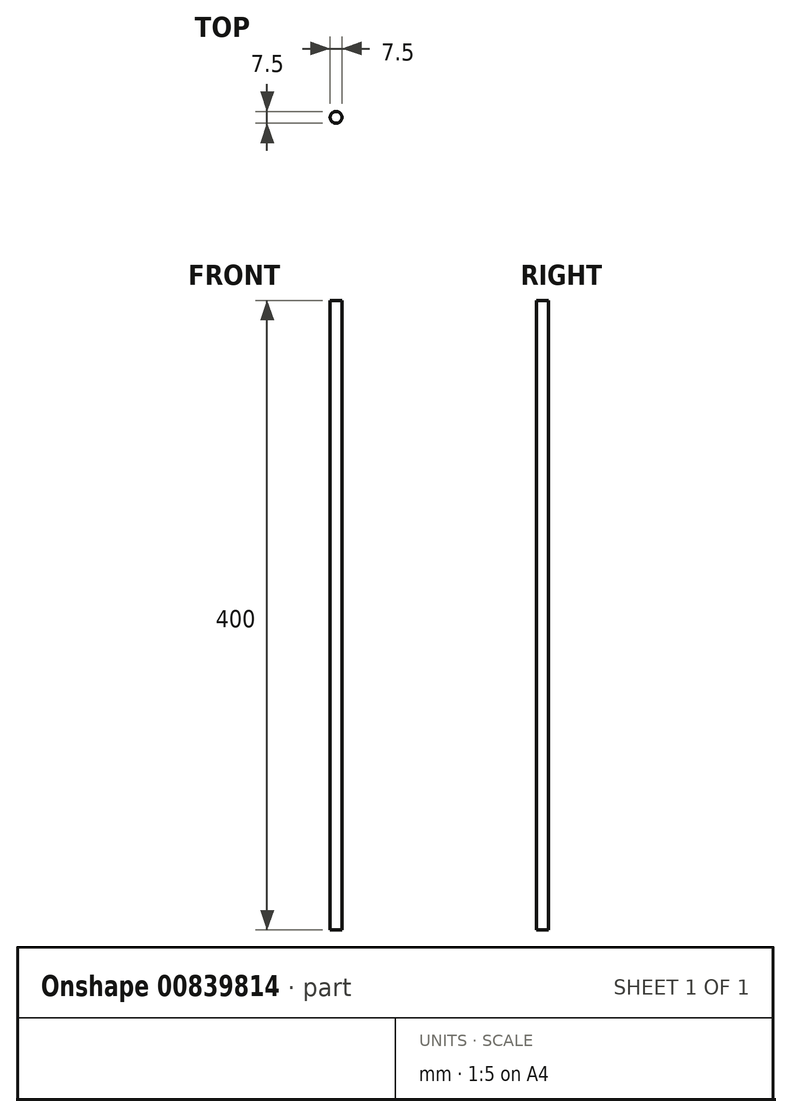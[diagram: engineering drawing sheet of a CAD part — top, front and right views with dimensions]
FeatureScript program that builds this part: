
annotation { "Feature Type Name" : "Feature", "Feature Type Description" : "" }
export const myFeature = defineFeature(function(context is Context, id is Id, definition is map)
    precondition{}
    {
        {
            var Q0;
            Q0=qCreatedBy(makeId("Front.planeOp"),FACE);
            var sketch = newSketch(context, id + "F0", { "sketchPlane" : qUnion([Q0])});
            skLineSegment(sketch, "E0.bottom", {"start": v(3.75, -400) * mm, "end": v(0, -400) * mm});
            skLineSegment(sketch, "E0.top", {"start": v(3.75, 0) * mm, "end": v(0, 0) * mm});
            skLineSegment(sketch, "E0.left", {"start": v(3.75, -400) * mm, "end": v(3.75, 0) * mm});
            skLineSegment(sketch, "E0.right", {"start": v(0, -400) * mm, "end": v(0, 0) * mm});
            skSolve(sketch);
        }
        {
            var Q0;
            Q0=makeQuery(id+"F0.imprint","IMPRINT",FACE,{"disambiguationData":[TD([[makeQuery(id+"F0.imprint","IMPRINT",EDGE,{"derivedFrom":sQuery(id+"F0.wireOp",EDGE,"E0.bottom")}),-1.0]])]});
            var Q1;
            Q1=sQuery(id+"F0.wireOp",EDGE,"E0.right");
            revolve(context, id + "F1", {"surfaceOperationType" : NewSurfaceOperationType.NEW, "entities" : qUnion([Q0]), "axis" : qUnion([Q1]), "revolveType" : RevolveType.FULL});
        }
    });
